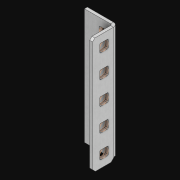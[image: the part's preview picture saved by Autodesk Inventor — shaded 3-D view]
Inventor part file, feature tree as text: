
AUTODESK INVENTOR PART (.ipt)
format: ipt  version: 2021 (Build 250183000, 183)  size: 1,048,064 bytes
history: native  units: in
note: dims shown in document units (in); Inventor stores cm internally (conversion verified against a paired STEP export)
features: extrude x12, other x10, sketch x4, pattern_linear x2, sheet_metal_op x1
ambient origin geometry x8: Origin, YZ Plane, XZ Plane, XY Plane, X Axis, Y Axis, Z Axis, Center Point
bodies: Solid1 (feature_tree)
feature tree (29):
  pattern_linear  "Rectangular Pattern1"  Spacing1=0.5in  [1 undecoded]
  pattern_linear  "Rectangular Pattern3"  Count1=5  [1 undecoded]
  extrude  "Extrusion1"  Depth=0.5in
  extrude  "Extrusion2"  Depth=0.5in
  sketch  "Sketch1"  dims[d0=0.182in]
  other  "Srf1"
  sketch  "Sketch3"  dims[d1=0.063in d2=0.0in]
  other  "Srf3"
  other  "Srf4"
  other  "Srf5"
  other  "Srf6"
  other  "Srf7"
  other  "Srf142"
  other  "Srf143"
  other  "Srf144"
  other  "Srf145"
  sketch  "Sketch4"  dims[d6=0.182in]
  sketch  "Sketch5"  dims[d7=0.063in d8=0.0in d11=0.5in d12=0.3937in d14=0.5in d18=1.9685in d20=0.5in d21=15.0in d22=0.0in d23=0.841in d24=0.0in]
  sheet_metal_op  "Fold1"
  extrude  "ExtrusionSrf1"  TaperAngle=0.0deg  [1 undecoded]
  extrude  "ExtrusionSrf3"  Depth=0.5in TaperAngle=0.0deg
  extrude  "ExtrusionSrf4"  [1 undecoded]
  extrude  "ExtrusionSrf5"  [1 undecoded]
  extrude  "ExtrusionSrf6"  [1 undecoded]
  extrude  "ExtrusionSrf7"  [1 undecoded]
  extrude  "ExtrusionSrf142"  [1 undecoded]
  extrude  "ExtrusionSrf143"  [1 undecoded]
  extrude  "ExtrusionSrf144"  [1 undecoded]
  extrude  "ExtrusionSrf145"  [1 undecoded]
note: 11 required parameter values undecoded (feature->parameter linkage not recoverable at this tier; creation-order binding heuristic only, values carry confidence <= 0.55)
